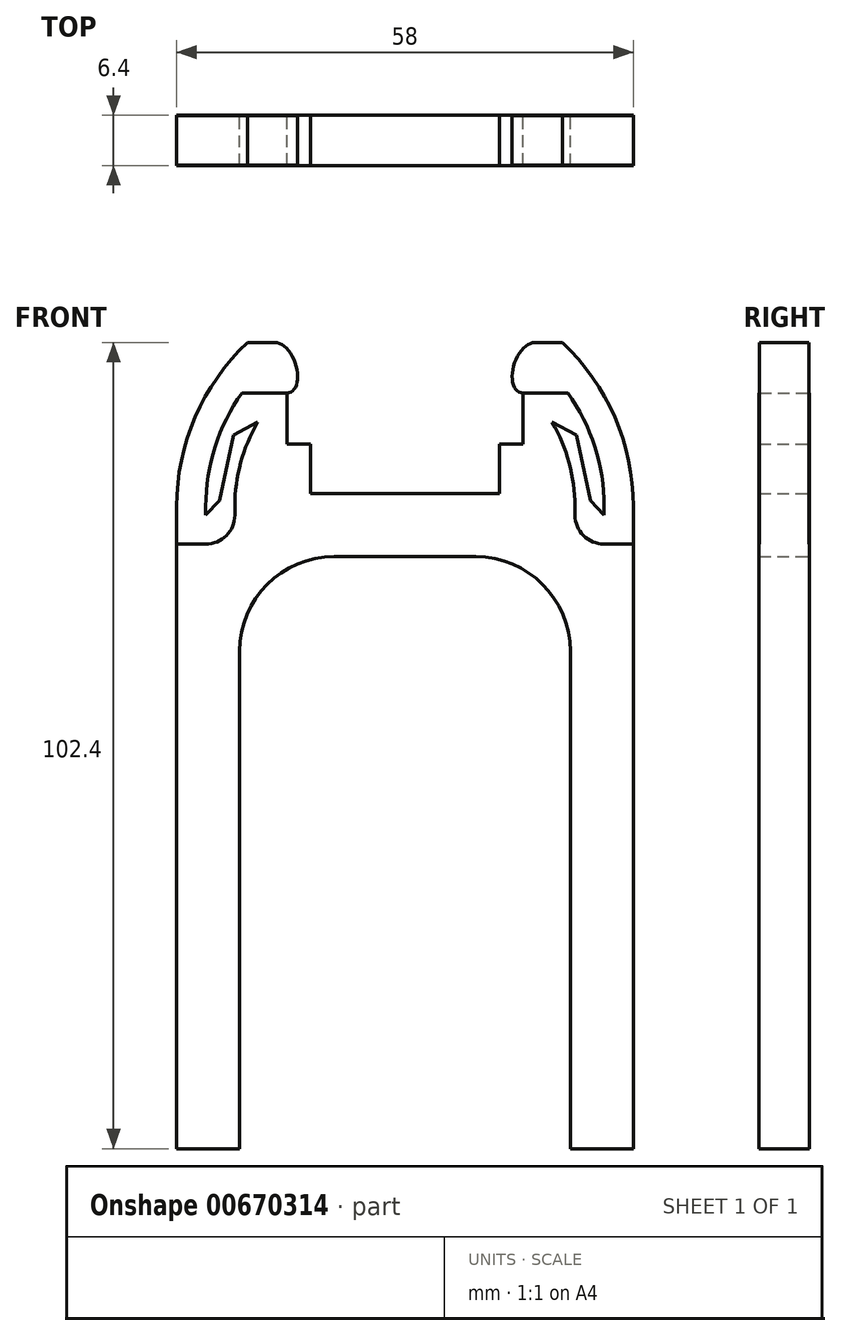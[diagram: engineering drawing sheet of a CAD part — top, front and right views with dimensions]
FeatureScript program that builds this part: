
annotation { "Feature Type Name" : "Feature", "Feature Type Description" : "" }
export const myFeature = defineFeature(function(context is Context, id is Id, definition is map)
    precondition{}
    {
        {
            assignVariable(context, id + "F0", {"name" : "thickness", "anyValue" : 6.4});
        }
        {
            var Q0;
            Q0=qCreatedBy(makeId("Front.planeOp"),FACE);
            var sketch = newSketch(context, id + "F1", { "sketchPlane" : qUnion([Q0])});
            skLineSegment(sketch, "E0", {"start": v(12, 0) * mm, "end": v(-12, 0) * mm});
            skLineSegment(sketch, "E1", {"start": v(-12, 0) * mm, "end": v(-12, 6.3) * mm});
            skLineSegment(sketch, "E2", {"start": v(-12, 6.3) * mm, "end": v(-15, 6.3) * mm});
            skLineSegment(sketch, "E3", {"start": v(-16.5, 19.2) * mm, "end": v(-20, 19.2) * mm});
            skLineSegment(sketch, "E4", {"start": v(12, 0) * mm, "end": v(12, 6.3) * mm});
            skLineSegment(sketch, "E5", {"start": v(12, 6.3) * mm, "end": v(15, 6.3) * mm});
            skLineSegment(sketch, "E6", {"start": v(16.5, 19.2) * mm, "end": v(20, 19.2) * mm});
            skArc(sketch, "E7", {"start": v(-29, -1.6) * mm, "mid": v(-26.65, 9.73) * mm, "end": v(-20, 19.2) * mm});
            skArc(sketch, "E8", {"start": v(29, -1.6) * mm, "mid": v(26.65, 9.73) * mm, "end": v(20, 19.2) * mm});
            skPoint(sketch, "E9", {"position": v(-16.5, 19.2) * mm});
            skPoint(sketch, "E10", {"position": v(-15, 12.8) * mm});
            skLineSegment(sketch, "E11", {"start": v(-15, 12.8) * mm, "end": v(-15, 6.3) * mm});
            skPoint(sketch, "E12", {"position": v(16.5, 19.2) * mm});
            skPoint(sketch, "E13", {"position": v(15, 12.8) * mm});
            skLineSegment(sketch, "E14", {"start": v(15, 12.8) * mm, "end": v(15, 6.3) * mm});
            skPoint(sketch, "E15", {"position": v(-20.7, 12.8) * mm});
            skLineSegment(sketch, "E16", {"start": v(-20.7, 12.8) * mm, "end": v(-15, 12.8) * mm});
            skArc(sketch, "E17", {"start": v(-20.7, 12.8) * mm, "mid": v(-24.12, 5.96) * mm, "end": v(-25.3, -1.6) * mm});
            skPoint(sketch, "E18", {"position": v(25.3, -1.6) * mm});
            skPoint(sketch, "E19", {"position": v(20.7, 12.8) * mm});
            skLineSegment(sketch, "E20", {"start": v(20.7, 12.8) * mm, "end": v(15, 12.8) * mm});
            skArc(sketch, "E21", {"start": v(25.3, -1.6) * mm, "mid": v(24.12, 5.96) * mm, "end": v(20.7, 12.8) * mm});
            skEllipticalArc(sketch, "E22", {});
            skPoint(sketch, "E23", {"position": v(-13.75, 16) * mm});
            skEllipticalArc(sketch, "E24", {});
            skPoint(sketch, "E25", {"position": v(13.75, 16) * mm});
            skLineSegment(sketch, "E26", {"start": v(-29, -1.6) * mm, "end": v(-29, -83.2) * mm});
            skLineSegment(sketch, "E27", {"start": v(-29, -83.2) * mm, "end": v(-21, -83.2) * mm});
            skLineSegment(sketch, "E28", {"start": v(-21, -83.2) * mm, "end": v(-21, -20) * mm});
            skLineSegment(sketch, "E29", {"start": v(-9, -8) * mm, "end": v(9, -8) * mm});
            skLineSegment(sketch, "E30", {"start": v(21, -20) * mm, "end": v(21, -83.2) * mm});
            skLineSegment(sketch, "E31", {"start": v(21, -83.2) * mm, "end": v(29, -83.2) * mm});
            skLineSegment(sketch, "E32", {"start": v(29, -83.2) * mm, "end": v(29, -1.6) * mm});
            skLineSegment(sketch, "E33", {"start": v(-25.3, -1.6) * mm, "end": v(-25.3, -2.7) * mm});
            skPoint(sketch, "E34.visualSharp", {"position": v(-21, -8) * mm});
            skArc(sketch, "E34.filletArc", {"start": v(-9, -8) * mm, "mid": v(-17.49, -11.51) * mm, "end": v(-21, -20) * mm});
            skPoint(sketch, "E35.visualSharp", {"position": v(21, -8) * mm});
            skArc(sketch, "E35.filletArc", {"start": v(21, -20) * mm, "mid": v(17.49, -11.51) * mm, "end": v(9, -8) * mm});
            skArc(sketch, "E36", {"start": v(-21.6, -1.6) * mm, "mid": v(-20.86, 3.94) * mm, "end": v(-18.7, 9.09) * mm});
            skLineSegment(sketch, "E37", {"start": v(-21.6, -2.7) * mm, "end": v(-21.6, -1.6) * mm});
            skLineSegment(sketch, "E38", {"start": v(-29, -6.4) * mm, "end": v(-25.3, -6.4) * mm});
            skArc(sketch, "E39", {"start": v(-25.3, -6.4) * mm, "mid": v(-22.68, -5.32) * mm, "end": v(-21.6, -2.7) * mm});
            skLineSegment(sketch, "E40", {"start": v(-25.3, -2.7) * mm, "end": v(-23.56, -0.88) * mm});
            skLineSegment(sketch, "E41", {"start": v(-23.56, -0.88) * mm, "end": v(-21.8, 7.46) * mm});
            skLineSegment(sketch, "E42", {"start": v(-21.8, 7.46) * mm, "end": v(-18.7, 9.09) * mm});
            skLineSegment(sketch, "E43", {"start": v(29, -6.4) * mm, "end": v(25.3, -6.4) * mm});
            skArc(sketch, "E44", {"start": v(25.3, -6.4) * mm, "mid": v(22.68, -5.32) * mm, "end": v(21.6, -2.7) * mm});
            skLineSegment(sketch, "E45", {"start": v(25.3, -2.7) * mm, "end": v(25.3, -1.6) * mm});
            skLineSegment(sketch, "E46", {"start": v(21.6, -2.7) * mm, "end": v(21.6, -1.6) * mm});
            skArc(sketch, "E47", {"start": v(21.6, -1.6) * mm, "mid": v(20.86, 3.94) * mm, "end": v(18.7, 9.09) * mm});
            skLineSegment(sketch, "E48", {"start": v(18.7, 9.09) * mm, "end": v(21.8, 7.46) * mm});
            skLineSegment(sketch, "E49", {"start": v(21.8, 7.46) * mm, "end": v(23.56, -0.88) * mm});
            skLineSegment(sketch, "E50", {"start": v(23.56, -0.88) * mm, "end": v(25.3, -2.7) * mm});
            const initialGuessF1  = {"E22": [-0.01575, 0.016, 0.34376296214879487, -0.9390564550945202, 0.003334452668927298, 0.0019193554791284218, 6.075507116165239, 2.933914424857674], "E24": [0.01575, 0.016, 0.34376294204844415, 0.9390564624527101, 0.003334452653566494, 0.0019193554517733936, 0.20767817569025931, 3.3492708292800506]};
            skSetInitialGuess(sketch, initialGuessF1);
            skSolve(sketch);
        }
        {
            var Q0;
            Q0=makeQuery(id+"F1.imprint","IMPRINT",FACE,{"disambiguationData":[TD([[makeQuery(id+"F1.imprint","IMPRINT",EDGE,{"derivedFrom":sQuery(id+"F1.wireOp",EDGE,"E0")}),1.0]])]});
            extrude(context, id + "F2", {"entities" : qUnion([Q0]), "endBound" : BoundingType.SYMMETRIC, "depth" : (getVariable(context, 'thickness')) * mm, "offsetDistance" : 25 * mm});
        }
        {
            var Q0;
            Q0=makeQuery(id+"F1.imprint","IMPRINT",FACE,{"disambiguationData":[TD([[makeQuery(id+"F1.imprint","IMPRINT",EDGE,{"derivedFrom":sQuery(id+"F1.wireOp",EDGE,"E3")}),1.0]])]});
            var Q1;
            Q1=makeQuery(id+"F1.imprint","IMPRINT",FACE,{"disambiguationData":[TD([[makeQuery(id+"F1.imprint","IMPRINT",EDGE,{"derivedFrom":sQuery(id+"F1.wireOp",EDGE,"E6")}),-1.0]])]});
            extrude(context, id + "F3", {"entities" : qUnion([Q0, Q1]), "operationType" : NewBodyOperationType.ADD, "endBound" : BoundingType.SYMMETRIC, "depth" : (getVariable(context, 'thickness') - 0.1) * mm, "offsetDistance" : 25 * mm});
        }
    });
